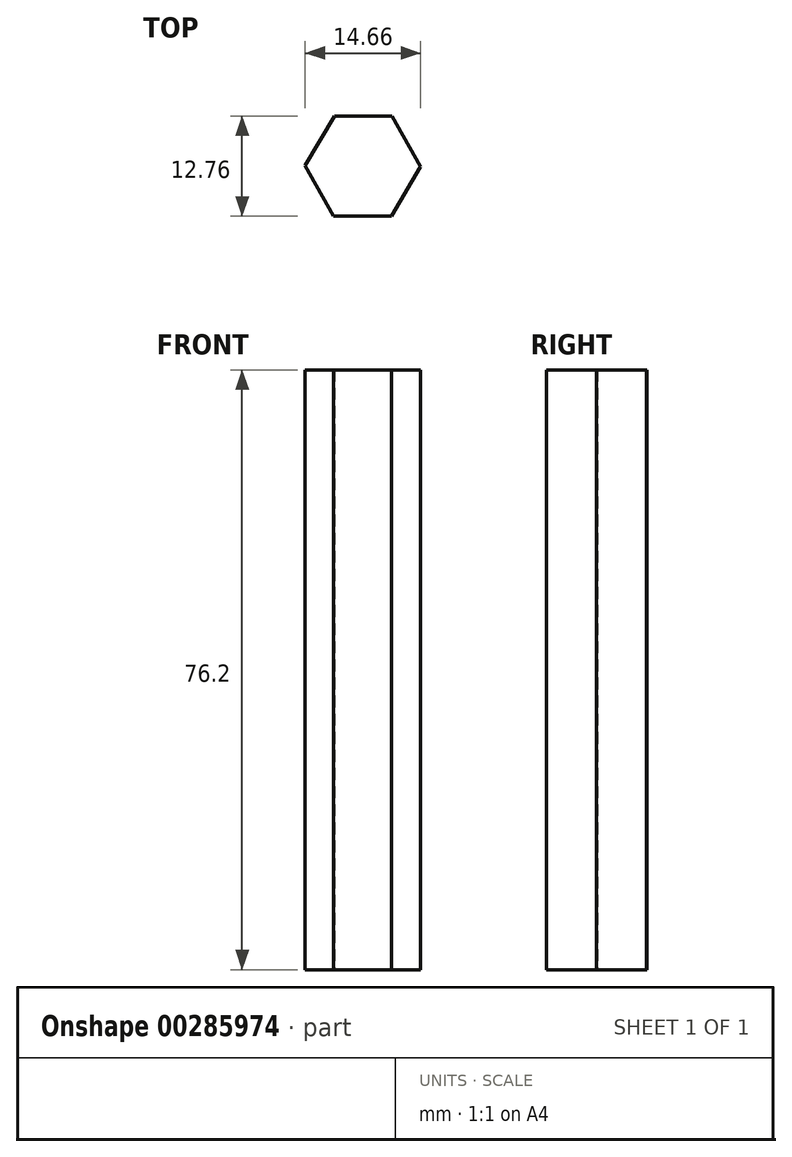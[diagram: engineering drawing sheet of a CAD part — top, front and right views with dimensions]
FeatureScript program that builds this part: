
annotation { "Feature Type Name" : "Feature", "Feature Type Description" : "" }
export const myFeature = defineFeature(function(context is Context, id is Id, definition is map)
    precondition{}
    {
        {
            var Q0;
            Q0=qCreatedBy(makeId("Top.planeOp"),FACE);
            var sketch = newSketch(context, id + "F0", { "sketchPlane" : qUnion([Q0])});
            skCircle(sketch, "E0.cCircle", {"center": v(0, 0) * mm, "radius": 6.35 * mm, "construction": true});
            skLineSegment(sketch, "E0.0", {"start": v(3.72, 6.32) * mm, "end": v(7.33, -0.06) * mm});
            skLineSegment(sketch, "E0.1", {"start": v(7.33, -0.06) * mm, "end": v(3.61, -6.38) * mm});
            skLineSegment(sketch, "E0.2", {"start": v(3.61, -6.38) * mm, "end": v(-3.72, -6.32) * mm});
            skLineSegment(sketch, "E0.3", {"start": v(-3.72, -6.32) * mm, "end": v(-7.33, 0.06) * mm});
            skLineSegment(sketch, "E0.4", {"start": v(-7.33, 0.06) * mm, "end": v(-3.61, 6.38) * mm});
            skLineSegment(sketch, "E0.5", {"start": v(-3.61, 6.38) * mm, "end": v(3.72, 6.32) * mm});
            skPoint(sketch, "E0.0.midPoint", {"position": v(5.52, 3.13) * mm});
            skSolve(sketch);
        }
        {
            var Q0;
            Q0 = qSketchRegion(id + "F0", true);
            extrude(context, id + "F1", {"entities" : qUnion([Q0]), "depth" : 76.2 * mm});
        }
    });
